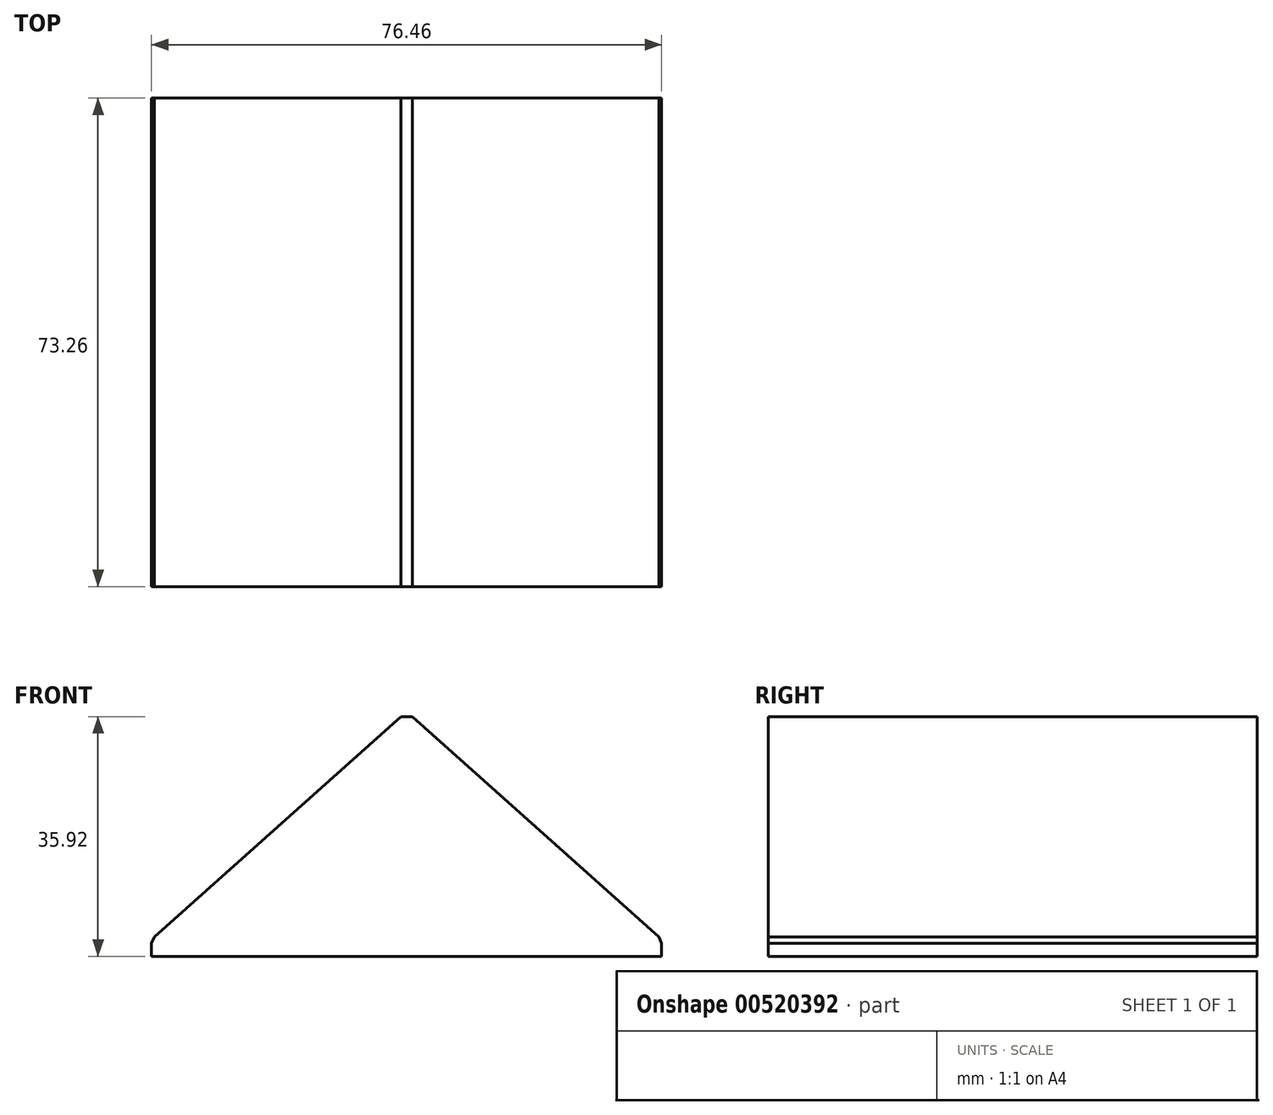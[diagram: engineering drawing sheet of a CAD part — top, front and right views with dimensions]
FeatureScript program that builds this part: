
annotation { "Feature Type Name" : "Feature", "Feature Type Description" : "" }
export const myFeature = defineFeature(function(context is Context, id is Id, definition is map)
    precondition{}
    {
        {
            var Q0;
            Q0=qCreatedBy(makeId("Top.planeOp"),FACE);
            var sketch = newSketch(context, id + "F0", { "sketchPlane" : qUnion([Q0])});
            skLineSegment(sketch, "E0", {"start": v(0, -36.63) * mm, "end": v(0, 0) * mm});
            skLineSegment(sketch, "E1", {"start": v(0, 0) * mm, "end": v(0, -73.26) * mm});
            skLineSegment(sketch, "E2", {"start": v(0, -36.63) * mm, "end": v(-38.23, -36.63) * mm});
            skLineSegment(sketch, "E3", {"start": v(0, -36.63) * mm, "end": v(38.23, -36.63) * mm});
            skLineSegment(sketch, "E4", {"start": v(38.23, -36.63) * mm, "end": v(38.23, -73.26) * mm});
            skLineSegment(sketch, "E5", {"start": v(38.23, -73.26) * mm, "end": v(0, -73.26) * mm});
            skLineSegment(sketch, "E6", {"start": v(0, -73.26) * mm, "end": v(-38.23, -73.26) * mm});
            skLineSegment(sketch, "E7", {"start": v(-38.23, -73.26) * mm, "end": v(-38.23, -36.63) * mm});
            skLineSegment(sketch, "E8", {"start": v(0, 0) * mm, "end": v(38.23, 0) * mm});
            skLineSegment(sketch, "E9", {"start": v(0, 0) * mm, "end": v(-38.23, 0) * mm});
            skLineSegment(sketch, "E10", {"start": v(38.23, 0) * mm, "end": v(38.23, -36.63) * mm});
            skLineSegment(sketch, "E11", {"start": v(-38.23, 0) * mm, "end": v(-38.23, -36.63) * mm});
            skSolve(sketch);
        }
        {
            var Q0;
            Q0 = qSketchRegion(id + "F0", true);
            extrude(context, id + "F1", {"entities" : qUnion([Q0]), "depth" : 2.54 * mm, "offsetDistance" : 25.4 * mm});
        }
        {
            var Q0;
            Q0=qCreatedBy(makeId("Front.planeOp"),FACE);
            var sketch = newSketch(context, id + "F2", { "sketchPlane" : qUnion([Q0])});
            skPoint(sketch, "E12.0", {"position": v(-38.23, 2.54) * mm});
            skLineSegment(sketch, "E13.0", {"start": v(38.23, 2.54) * mm, "end": v(-38.23, 2.54) * mm});
            skLineSegment(sketch, "E14", {"start": v(-38.23, 2.54) * mm, "end": v(0, 36.68) * mm});
            skLineSegment(sketch, "E15", {"start": v(0, 36.68) * mm, "end": v(38.23, 2.54) * mm});
            skSolve(sketch);
        }
        {
            var Q0;
            Q0 = qSketchRegion(id + "F2", true);
            extrude(context, id + "F3", {"entities" : qUnion([Q0]), "operationType" : NewBodyOperationType.ADD, "depth" : 73.26 * mm, "offsetDistance" : 25.4 * mm});
        }
        {
            var Q0;
            Q0=makeQuery(id+"F3.boolean.opBoolean","MERGE",EDGE,{"derivedFrom":[makeQuery(id+"F1.opExtrude","CAP_EDGE",EDGE,{"disambiguationData":[OSD([sQuery(id+"F0.wireOp",EDGE,"E4"),sQuery(id+"F0.wireOp",EDGE,"E10")])],"isStart":false}),makeQuery(id+"F3.opExtrude","SWEPT_EDGE",EDGE,{"disambiguationData":[OSD([sQuery(id+"F2.wireOp",EDGE,"E13.0"),sQuery(id+"F2.wireOp",EDGE,"E15")])]})]});
            var Q1;
            Q1=makeQuery(id+"F3.opExtrude","SWEPT_EDGE",EDGE,{"disambiguationData":[OSD([sQuery(id+"F2.wireOp",EDGE,"E14"),sQuery(id+"F2.wireOp",EDGE,"E15")])]});
            var Q2;
            Q2=makeQuery(id+"F3.boolean.opBoolean","MERGE",EDGE,{"derivedFrom":[makeQuery(id+"F1.opExtrude","CAP_EDGE",EDGE,{"disambiguationData":[OSD([sQuery(id+"F0.wireOp",EDGE,"E7"),sQuery(id+"F0.wireOp",EDGE,"E11")])],"isStart":false}),makeQuery(id+"F3.opExtrude","SWEPT_EDGE",EDGE,{"disambiguationData":[OSD([sQuery(id+"F2.wireOp",EDGE,"E13.0"),sQuery(id+"F2.wireOp",EDGE,"E14")])]})]});
            chamfer(context, id + "F4", {"entities" : qUnion([Q0, Q1, Q2]), "width" : 1.27 * mm, "tangentPropagation" : true});
        }
    });
